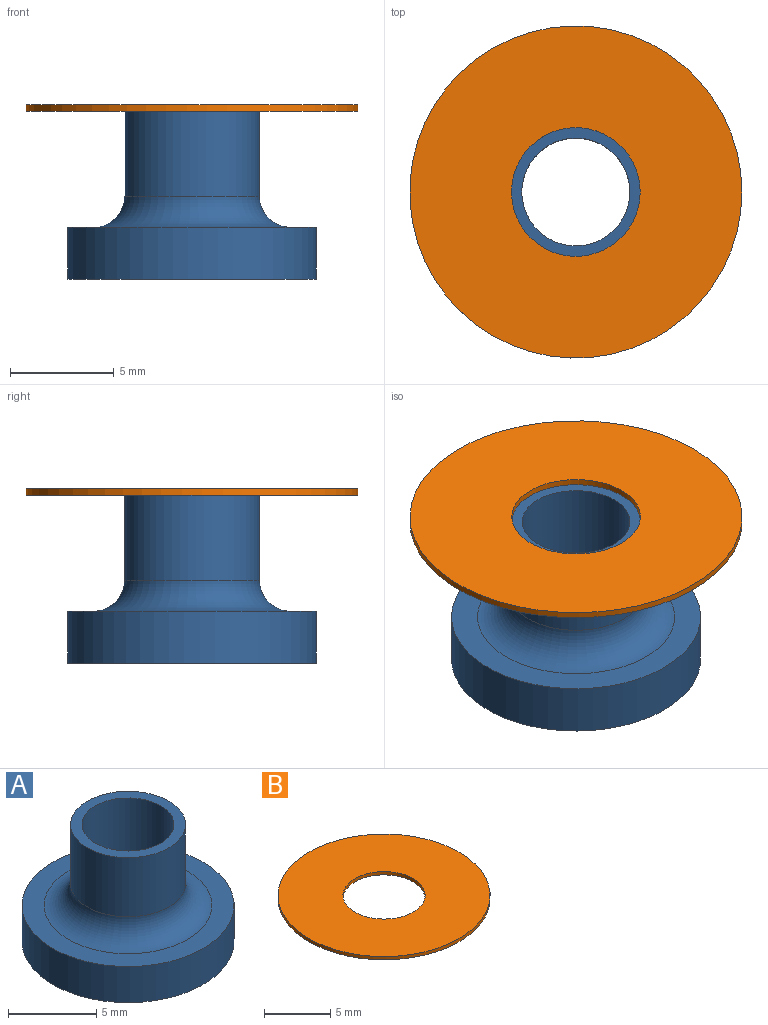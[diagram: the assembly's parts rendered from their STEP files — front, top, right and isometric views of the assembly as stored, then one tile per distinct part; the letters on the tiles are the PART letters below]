
ASSEMBLY  parts=2 mates=1
PART A: 7 faces, bbox 12.6x12.6x8.1 mm
  f0: cylinder r=2.6mm len=8.1mm, axis (0,0,-1), area 132.3mm2, adj f2,f3
  f1: cylinder r=3.25mm len=6.5mm, axis (0,0,-1), area 83.7mm2, adj f2,f6
  f2: plane 6.5x6.5mm, normal (0,0,1), area 11.9mm2, adj f0,f1
  f3: plane 12x12mm, normal (0,0,-1), area 91.9mm2, adj f0,f4
  f4: cylinder r=6mm len=12mm, axis (0,0,-1), area 94.2mm2, adj f3,f5
  f5: plane 12x12mm, normal (0,0,1), area 42.2mm2, adj f4,f6
  f6: torus R=4.75mm, axis (0,0,1), area 56.2mm2, adj f1,f5
PART B: 4 faces, bbox 16x16x0.3 mm
  f0: cylinder r=3.1mm len=6.2mm, axis (0,0,-1), area 5.8mm2, adj f2,f3
  f1: cylinder r=8mm len=16mm, axis (0,0,-1), area 15.1mm2, adj f2,f3
  f2: plane 16x16mm, normal (0,0,1), area 170.9mm2, adj f0,f1
  f3: plane 16x16mm, normal (0,0,-1), area 170.9mm2, adj f0,f1
PLACE A t=(-8.93,-4.6,-3.21)mm fixed
PLACE B t=(-8.93,-4.6,4.89)mm
MATE slider A.f1 <-> B.f1  axis (0,0,1) through (-8.93,-4.6,4.89)mm
